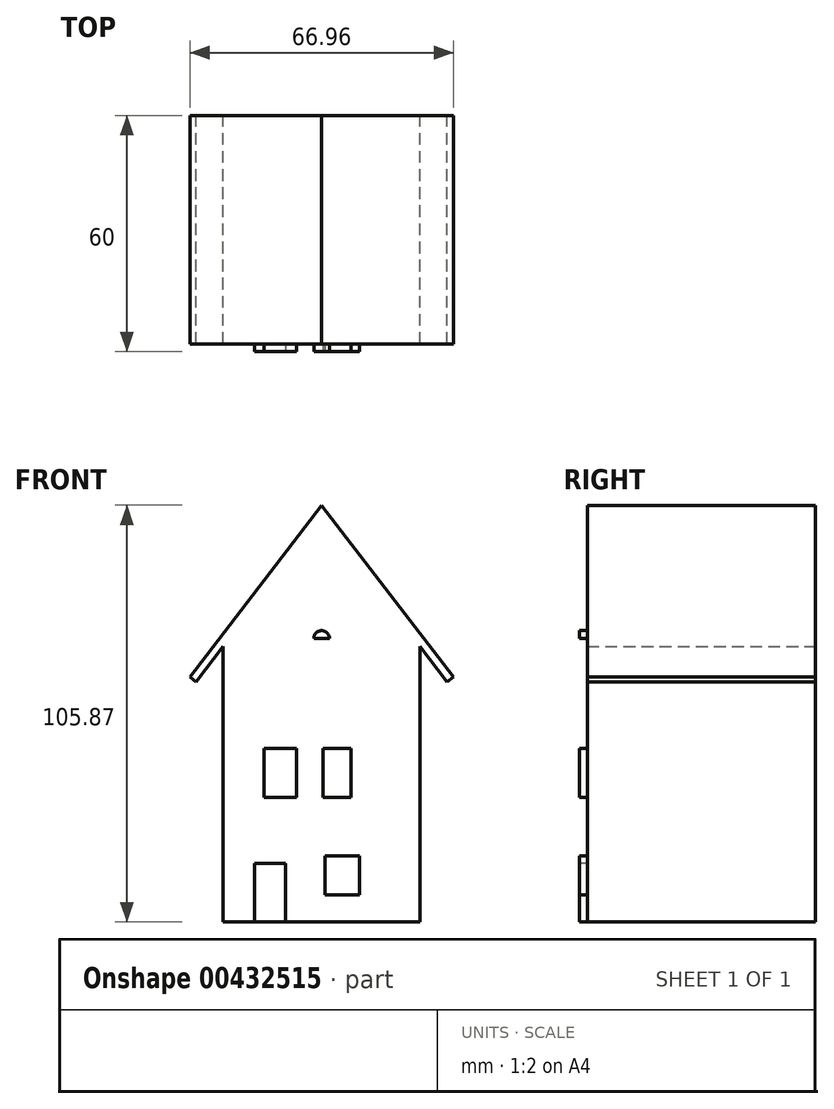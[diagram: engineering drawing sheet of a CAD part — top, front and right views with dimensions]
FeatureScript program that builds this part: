
annotation { "Feature Type Name" : "Feature", "Feature Type Description" : "" }
export const myFeature = defineFeature(function(context is Context, id is Id, definition is map)
    precondition{}
    {
        {
            var Q0;
            Q0=qCreatedBy(makeId("Front.planeOp"),FACE);
            var sketch = newSketch(context, id + "F0", { "sketchPlane" : qUnion([Q0])});
            skLineSegment(sketch, "E0", {"start": v(-25, 0) * mm, "end": v(-25, 70) * mm});
            skLineSegment(sketch, "E1", {"start": v(-25, 70) * mm, "end": v(0, 102.58) * mm});
            skLineSegment(sketch, "E2", {"start": v(-25, 0) * mm, "end": v(0, 0) * mm});
            skLineSegment(sketch, "E3.MirrorCS", {"start": v(25, 70) * mm, "end": v(0, 102.58) * mm});
            skLineSegment(sketch, "E4.MirrorCS", {"start": v(25, 0) * mm, "end": v(25, 70) * mm});
            skLineSegment(sketch, "E5.MirrorCS", {"start": v(25, 0) * mm, "end": v(0, 0) * mm});
            skSolve(sketch);
        }
        {
            var Q0;
            Q0 = qSketchRegion(id + "F0", true);
            extrude(context, id + "F1", {"entities" : qUnion([Q0]), "depth" : 30 * mm, "hasSecondDirection" : true, "secondDirectionOppositeDirection" : true, "secondDirectionDepth" : 30 * mm});
        }
        {
            var Q0;
            Q0=qCreatedBy(makeId("Front.planeOp"),FACE);
            var sketch = newSketch(context, id + "F2", { "sketchPlane" : qUnion([Q0])});
            skLineSegment(sketch, "E6", {"start": v(-31.9, 61.01) * mm, "end": v(0, 102.58) * mm});
            skLineSegment(sketch, "E7.MirrorCS", {"start": v(31.9, 61.01) * mm, "end": v(0, 102.58) * mm});
            skLineSegment(sketch, "E8.0", {"start": v(33.48, 62.23) * mm, "end": v(0, 105.87) * mm});
            skLineSegment(sketch, "E8.1", {"start": v(-33.48, 62.23) * mm, "end": v(0, 105.87) * mm});
            skLineSegment(sketch, "E9", {"start": v(-33.48, 62.23) * mm, "end": v(-31.9, 61.01) * mm});
            skLineSegment(sketch, "E10", {"start": v(31.9, 61.01) * mm, "end": v(33.48, 62.23) * mm});
            skSolve(sketch);
        }
        {
            var Q0;
            Q0 = qSketchRegion(id + "F2", true);
            extrude(context, id + "F3", {"entities" : qUnion([Q0]), "operationType" : NewBodyOperationType.ADD, "depth" : 30 * mm, "hasSecondDirection" : true, "secondDirectionOppositeDirection" : true, "secondDirectionDepth" : 30 * mm});
        }
        {
            var Q0;
            Q0=makeQuery(id+"F3.boolean.opBoolean","MERGE",FACE,{"derivedFrom":[makeQuery(id+"F1.opExtrude","CAP_FACE",FACE,{"disambiguationData":[OSD([sQuery(id+"F0.wireOp",EDGE,"E0"),sQuery(id+"F0.wireOp",EDGE,"E1"),sQuery(id+"F0.wireOp",EDGE,"E2"),sQuery(id+"F0.wireOp",EDGE,"E3.MirrorCS"),sQuery(id+"F0.wireOp",EDGE,"E4.MirrorCS"),sQuery(id+"F0.wireOp",EDGE,"E5.MirrorCS")])],"isStart":false}),makeQuery(id+"F3.opExtrude","CAP_FACE",FACE,{"disambiguationData":[OSD([sQuery(id+"F2.wireOp",EDGE,"E6"),sQuery(id+"F2.wireOp",EDGE,"E7.MirrorCS"),sQuery(id+"F2.wireOp",EDGE,"E8.0"),sQuery(id+"F2.wireOp",EDGE,"E8.1"),sQuery(id+"F2.wireOp",EDGE,"E9"),sQuery(id+"F2.wireOp",EDGE,"E10")])],"isStart":false})]});
            var sketch = newSketch(context, id + "F4", { "sketchPlane" : qUnion([Q0])});
            skLineSegment(sketch, "E11.bottom", {"start": v(-17.01, 14.93) * mm, "end": v(-9.14, 14.93) * mm});
            skLineSegment(sketch, "E11.top", {"start": v(-17.01, 0) * mm, "end": v(-9.14, 0) * mm});
            skLineSegment(sketch, "E11.left", {"start": v(-17.01, 14.93) * mm, "end": v(-17.01, 0) * mm});
            skLineSegment(sketch, "E11.right", {"start": v(-9.14, 14.93) * mm, "end": v(-9.14, 0) * mm});
            skLineSegment(sketch, "E12.bottom", {"start": v(-14.7, 44.08) * mm, "end": v(-6.37, 44.08) * mm});
            skLineSegment(sketch, "E12.top", {"start": v(-14.7, 31.59) * mm, "end": v(-6.37, 31.59) * mm});
            skLineSegment(sketch, "E12.left", {"start": v(-14.7, 44.08) * mm, "end": v(-14.7, 31.59) * mm});
            skLineSegment(sketch, "E12.right", {"start": v(-6.37, 44.08) * mm, "end": v(-6.37, 31.59) * mm});
            skLineSegment(sketch, "E13.bottom", {"start": v(0.34, 44.08) * mm, "end": v(7.52, 44.08) * mm});
            skLineSegment(sketch, "E13.top", {"start": v(0.34, 31.59) * mm, "end": v(7.52, 31.59) * mm});
            skLineSegment(sketch, "E13.left", {"start": v(0.34, 44.08) * mm, "end": v(0.34, 31.59) * mm});
            skLineSegment(sketch, "E13.right", {"start": v(7.52, 44.08) * mm, "end": v(7.52, 31.59) * mm});
            skLineSegment(sketch, "E14.bottom", {"start": v(0.8, 16.78) * mm, "end": v(9.6, 16.78) * mm});
            skLineSegment(sketch, "E14.top", {"start": v(0.8, 6.83) * mm, "end": v(9.6, 6.83) * mm});
            skLineSegment(sketch, "E14.left", {"start": v(0.8, 16.78) * mm, "end": v(0.8, 6.83) * mm});
            skLineSegment(sketch, "E14.right", {"start": v(9.6, 16.78) * mm, "end": v(9.6, 6.83) * mm});
            skLineSegment(sketch, "E15", {"start": v(-7, 72) * mm, "end": v(7, 72) * mm, "construction": true});
            skArc(sketch, "E16", {"start": v(-7, 72) * mm, "mid": v(0, 79) * mm, "end": v(7, 72) * mm, "construction": true});
            skArc(sketch, "E17", {"start": v(-3, 72) * mm, "mid": v(0, 75) * mm, "end": v(3, 72) * mm, "construction": true});
            skArc(sketch, "E18", {"start": v(-2, 72) * mm, "mid": v(0, 74) * mm, "end": v(2, 72) * mm, "construction": true});
            skLineSegment(sketch, "E19", {"start": v(0, 72) * mm, "end": v(-6.1, 75.43) * mm, "construction": true});
            skLineSegment(sketch, "E20", {"start": v(0, 72) * mm, "end": v(-5.55, 76.26) * mm, "construction": true});
            skLineSegment(sketch, "E21", {"start": v(0, 72) * mm, "end": v(-0.5, 78.98) * mm, "construction": true});
            skLineSegment(sketch, "E22.MirrorCS", {"start": v(0, 72) * mm, "end": v(6.1, 75.43) * mm, "construction": true});
            skLineSegment(sketch, "E23.MirrorCS", {"start": v(0, 72) * mm, "end": v(5.55, 76.26) * mm, "construction": true});
            skLineSegment(sketch, "E24.MirrorCS", {"start": v(0, 72) * mm, "end": v(0.5, 78.98) * mm, "construction": true});
            skLineSegment(sketch, "E25", {"start": v(-3, 72) * mm, "end": v(-7, 72) * mm});
            skLineSegment(sketch, "E26", {"start": v(-2.62, 73.47) * mm, "end": v(-6.1, 75.43) * mm});
            skLineSegment(sketch, "E27", {"start": v(-2.38, 73.83) * mm, "end": v(-5.55, 76.26) * mm});
            skLineSegment(sketch, "E28", {"start": v(-0.5, 78.98) * mm, "end": v(-0.21, 75) * mm});
            skLineSegment(sketch, "E29", {"start": v(0.5, 78.98) * mm, "end": v(0.21, 75) * mm});
            skLineSegment(sketch, "E30", {"start": v(5.55, 76.26) * mm, "end": v(2.38, 73.83) * mm});
            skLineSegment(sketch, "E31", {"start": v(6.1, 75.43) * mm, "end": v(2.62, 73.47) * mm});
            skLineSegment(sketch, "E32", {"start": v(3, 72) * mm, "end": v(7, 72) * mm});
            skArc(sketch, "E33", {"start": v(-7, 72) * mm, "mid": v(-6.77, 73.77) * mm, "end": v(-6.1, 75.43) * mm});
            skArc(sketch, "E34", {"start": v(-5.55, 76.26) * mm, "mid": v(-3.32, 78.16) * mm, "end": v(-0.5, 78.98) * mm});
            skArc(sketch, "E35", {"start": v(0.5, 78.98) * mm, "mid": v(3.32, 78.16) * mm, "end": v(5.55, 76.26) * mm});
            skArc(sketch, "E36", {"start": v(6.1, 75.43) * mm, "mid": v(6.77, 73.77) * mm, "end": v(7, 72) * mm});
            skArc(sketch, "E37", {"start": v(-2, 72) * mm, "mid": v(-1.93, 72.5) * mm, "end": v(-1.74, 72.98) * mm});
            skArc(sketch, "E38", {"start": v(-1.59, 73.22) * mm, "mid": v(-0.95, 73.76) * mm, "end": v(-0.14, 74) * mm});
            skArc(sketch, "E39", {"start": v(0.14, 74) * mm, "mid": v(0.95, 73.76) * mm, "end": v(1.59, 73.22) * mm});
            skArc(sketch, "E40", {"start": v(1.74, 72.98) * mm, "mid": v(1.93, 72.5) * mm, "end": v(2, 72) * mm});
            skLineSegment(sketch, "E41", {"start": v(0, 72) * mm, "end": v(2, 72) * mm});
            skLineSegment(sketch, "E42", {"start": v(0, 72) * mm, "end": v(-2, 72) * mm});
            skArc(sketch, "E43", {"start": v(-2.62, 73.47) * mm, "mid": v(-2.9, 72.76) * mm, "end": v(-3, 72) * mm});
            skArc(sketch, "E44", {"start": v(-2.38, 73.83) * mm, "mid": v(-1.42, 74.64) * mm, "end": v(-0.21, 75) * mm});
            skArc(sketch, "E45", {"start": v(0.21, 75) * mm, "mid": v(1.42, 74.64) * mm, "end": v(2.38, 73.83) * mm});
            skArc(sketch, "E46", {"start": v(2.62, 73.47) * mm, "mid": v(2.9, 72.76) * mm, "end": v(3, 72) * mm});
            skArc(sketch, "E47", {"start": v(-1.74, 72.98) * mm, "mid": v(-1.67, 73.1) * mm, "end": v(-1.59, 73.22) * mm});
            skArc(sketch, "E48", {"start": v(-0.14, 74) * mm, "mid": v(0, 74) * mm, "end": v(0.14, 74) * mm});
            skArc(sketch, "E49", {"start": v(1.59, 73.22) * mm, "mid": v(1.67, 73.1) * mm, "end": v(1.74, 72.98) * mm});
            skSolve(sketch);
        }
        {
            var Q0;
            Q0=makeQuery(id+"F4.imprint","IMPRINT",FACE,{"disambiguationData":[TD([[makeQuery(id+"F4.imprint","IMPRINT",EDGE,{"derivedFrom":sQuery(id+"F4.wireOp",EDGE,"E25")}),-1.0]])]});
            var Q1;
            Q1=makeQuery(id+"F4.imprint","IMPRINT",FACE,{"disambiguationData":[TD([[makeQuery(id+"F4.imprint","IMPRINT",EDGE,{"derivedFrom":sQuery(id+"F4.wireOp",EDGE,"E27")}),-1.0]])]});
            var Q2;
            Q2=makeQuery(id+"F4.imprint","IMPRINT",FACE,{"disambiguationData":[TD([[makeQuery(id+"F4.imprint","IMPRINT",EDGE,{"derivedFrom":sQuery(id+"F4.wireOp",EDGE,"E29")}),1.0]])]});
            var Q3;
            Q3=makeQuery(id+"F4.imprint","IMPRINT",FACE,{"disambiguationData":[TD([[makeQuery(id+"F4.imprint","IMPRINT",EDGE,{"derivedFrom":sQuery(id+"F4.wireOp",EDGE,"E31")}),1.0]])]});
            var Q4;
            Q4=makeQuery(id+"F4.imprint","IMPRINT",FACE,{"disambiguationData":[TD([[makeQuery(id+"F4.imprint","IMPRINT",EDGE,{"derivedFrom":sQuery(id+"F4.wireOp",EDGE,"E37")}),-1.0]])]});
            extrude(context, id + "F5", {"entities" : qUnion([Q0, Q1, Q2, Q3, Q4]), "operationType" : NewBodyOperationType.REMOVE, "oppositeDirection" : true, "depth" : 2 * mm});
        }
    });
